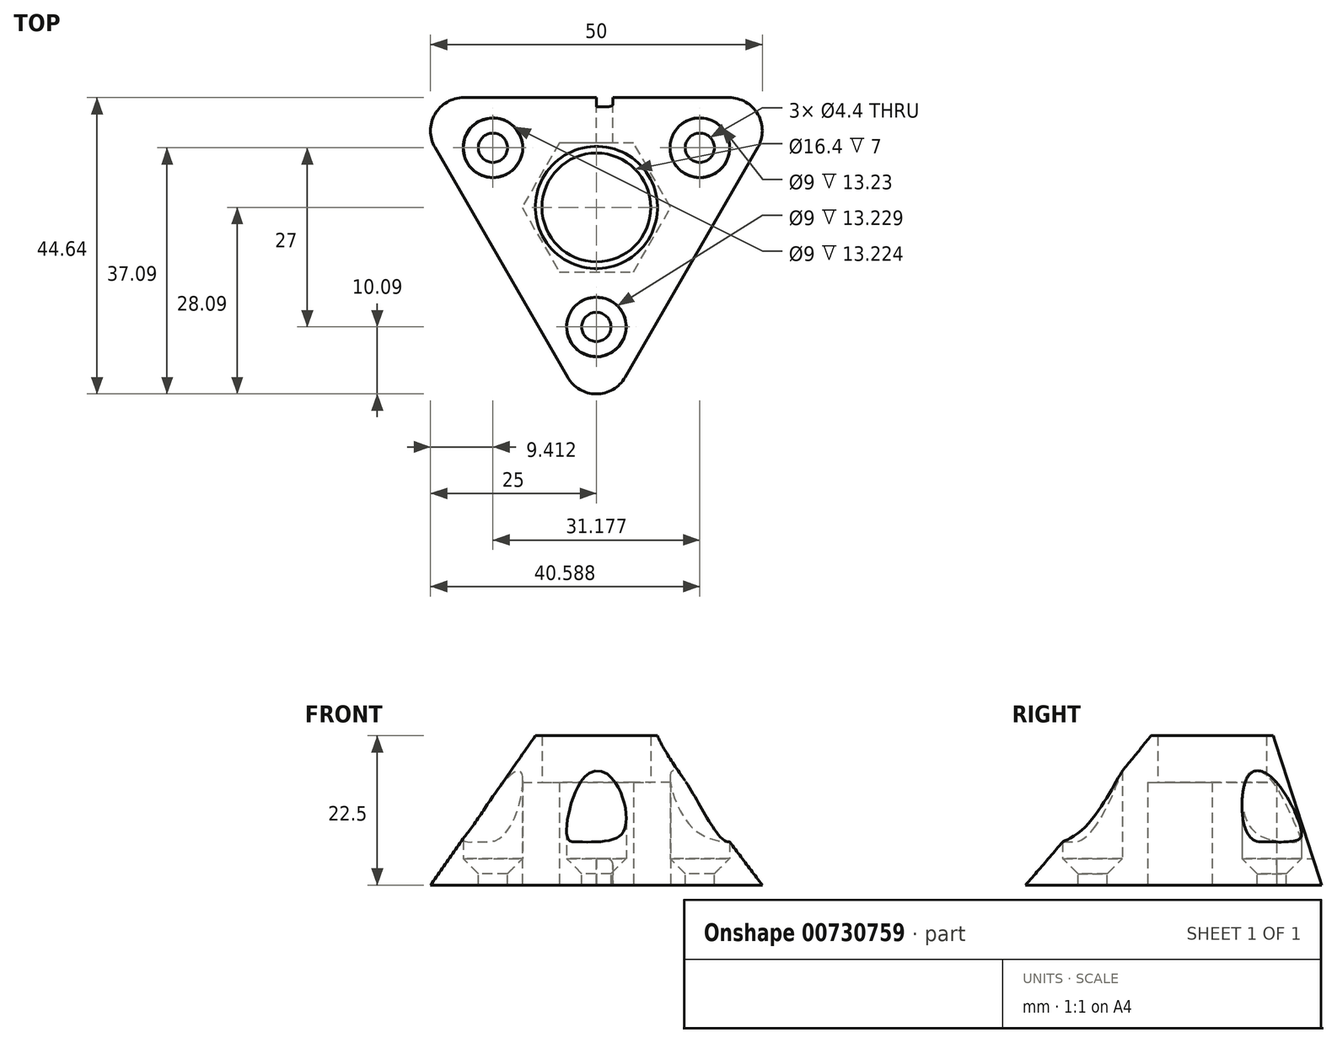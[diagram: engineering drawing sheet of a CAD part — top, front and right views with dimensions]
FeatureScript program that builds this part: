
annotation { "Feature Type Name" : "Feature", "Feature Type Description" : "" }
export const myFeature = defineFeature(function(context is Context, id is Id, definition is map)
    precondition{}
    {
        {
            var Q0;
            Q0=qCreatedBy(makeId("Top.planeOp"),FACE);
            var sketch = newSketch(context, id + "F0", { "sketchPlane" : qUnion([Q0])});
            skCircle(sketch, "E0.cCircle", {"center": v(0, 0) * mm, "radius": 16.55 * mm, "construction": true});
            skLineSegment(sketch, "E0.0", {"start": v(24.33, 9.05) * mm, "end": v(4.33, -25.6) * mm});
            skLineSegment(sketch, "E0.1", {"start": v(-4.33, -25.6) * mm, "end": v(-24.33, 9.05) * mm});
            skLineSegment(sketch, "E0.2", {"start": v(-20, 16.55) * mm, "end": v(20, 16.55) * mm});
            skPoint(sketch, "E0.0.midPoint", {"position": v(14.33, -8.27) * mm});
            skPoint(sketch, "E1.visualSharp", {"position": v(-28.66, 16.55) * mm});
            skArc(sketch, "E1.filletArc", {"start": v(-20, 16.55) * mm, "mid": v(-24.33, 14.05) * mm, "end": v(-24.33, 9.05) * mm});
            skPoint(sketch, "E2.visualSharp", {"position": v(28.66, 16.55) * mm});
            skArc(sketch, "E2.filletArc", {"start": v(24.33, 9.05) * mm, "mid": v(24.33, 14.05) * mm, "end": v(20, 16.55) * mm});
            skPoint(sketch, "E3.visualSharp", {"position": v(0, -33.1) * mm});
            skArc(sketch, "E3.filletArc", {"start": v(-4.33, -25.6) * mm, "mid": v(0, -28.1) * mm, "end": v(4.33, -25.6) * mm});
            skSolve(sketch);
        }
        {
            var Q0;
            Q0=qCreatedBy(makeId("Top.planeOp"),FACE);
            cPlane(context, id + "F1", {"entities" : qUnion([Q0]), "cplaneType" : CPlaneType.OFFSET, "offset" : 22.5 * mm, "width" : 150 * mm, "height" : 150 * mm});
        }
        {
            var Q0;
            Q0=qCreatedBy(id+"F1.planeOp",FACE);
            var sketch = newSketch(context, id + "F2", { "sketchPlane" : qUnion([Q0])});
            skCircle(sketch, "E4", {"center": v(0, 0) * mm, "radius": 9.2 * mm});
            skSolve(sketch);
        }
        {
            var Q0;
            Q0=makeQuery(id+"F0.imprint","IMPRINT",FACE,{"disambiguationData":[TD([[makeQuery(id+"F0.imprint","IMPRINT",EDGE,{"derivedFrom":sQuery(id+"F0.wireOp",EDGE,"E0.0")}),-1.0]])]});
            var Q1;
            Q1=makeQuery(id+"F2.imprint","IMPRINT",FACE,{"disambiguationData":[TD([[makeQuery(id+"F2.imprint","IMPRINT",EDGE,{"derivedFrom":sQuery(id+"F2.wireOp",EDGE,"E4")}),1.0]])]});
            loft(context, id + "F3", {"sheetProfilesArray" : [{ "sheetProfileEntities" : qUnion([Q0]) }, { "sheetProfileEntities" : qUnion([Q1]) }]});
        }
        {
            var Q0;
            Q0=makeQuery(id+"F3.opLoft","CAP_FACE",FACE,{"disambiguationData":[OSD([makeQuery(id+"F0.imprint","IMPRINT",FACE,{"disambiguationData":[TD([[makeQuery(id+"F0.imprint","IMPRINT",EDGE,{"derivedFrom":sQuery(id+"F0.wireOp",EDGE,"E0.0")}),-1.0]])]})])],"isStart":true});
            var sketch = newSketch(context, id + "F4", { "sketchPlane" : qUnion([Q0])});
            skCircle(sketch, "E5", {"center": v(0, 0) * mm, "radius": 8.2 * mm});
            skCircle(sketch, "E6.cCircle", {"center": v(0, 0) * mm, "radius": 9.7 * mm, "construction": true});
            skLineSegment(sketch, "E6.0", {"start": v(-5.6, 9.7) * mm, "end": v(5.6, 9.7) * mm});
            skLineSegment(sketch, "E6.1", {"start": v(5.6, 9.7) * mm, "end": v(11.2, 0) * mm});
            skLineSegment(sketch, "E6.2", {"start": v(11.2, 0) * mm, "end": v(5.6, -9.7) * mm});
            skLineSegment(sketch, "E6.3", {"start": v(5.6, -9.7) * mm, "end": v(-5.6, -9.7) * mm});
            skLineSegment(sketch, "E6.4", {"start": v(-5.6, -9.7) * mm, "end": v(-11.2, 0) * mm});
            skLineSegment(sketch, "E6.5", {"start": v(-11.2, 0) * mm, "end": v(-5.6, 9.7) * mm});
            skPoint(sketch, "E6.0.midPoint", {"position": v(0, 9.7) * mm});
            skLineSegment(sketch, "E7.bottom", {"start": v(0, -9.7) * mm, "end": v(-2.5, -9.7) * mm});
            skLineSegment(sketch, "E7.top", {"start": v(0, -16.55) * mm, "end": v(-2.5, -16.55) * mm});
            skLineSegment(sketch, "E7.left", {"start": v(0, -9.7) * mm, "end": v(0, -16.55) * mm});
            skLineSegment(sketch, "E7.right", {"start": v(-2.5, -9.7) * mm, "end": v(-2.5, -16.55) * mm});
            skLineSegment(sketch, "E8.MirrorCS", {"start": v(2.5, -9.7) * mm, "end": v(2.5, -16.55) * mm});
            skSolve(sketch);
        }
        {
            var Q0;
            Q0=makeQuery(id+"F4.imprint","IMPRINT",FACE,{"disambiguationData":[TD([[makeQuery(id+"F4.imprint","IMPRINT",EDGE,{"derivedFrom":sQuery(id+"F4.wireOp",EDGE,"E5")}),1.0]])]});
            extrude(context, id + "F5", {"entities" : qUnion([Q0]), "operationType" : NewBodyOperationType.REMOVE, "endBound" : BoundingType.UP_TO_NEXT, "oppositeDirection" : true, "depth" : 25 * mm, "offsetDistance" : 25 * mm});
        }
        {
            var Q0;
            Q0=makeQuery(id+"F4.imprint","IMPRINT",FACE,{"disambiguationData":[TD([[makeQuery(id+"F4.imprint","IMPRINT",EDGE,{"derivedFrom":sQuery(id+"F4.wireOp",EDGE,"E5")}),-1.0]])]});
            extrude(context, id + "F6", {"entities" : qUnion([Q0]), "operationType" : NewBodyOperationType.REMOVE, "oppositeDirection" : true, "depth" : 15.5 * mm, "offsetDistance" : 25 * mm});
        }
        {
            var Q0;
            Q0=qCreatedBy(makeId("Top.planeOp"),FACE);
            cPlane(context, id + "F7", {"entities" : qUnion([Q0]), "cplaneType" : CPlaneType.OFFSET, "offset" : 4 * mm, "width" : 150 * mm, "height" : 150 * mm});
        }
        {
            var Q0;
            Q0=qCreatedBy(id+"F7.planeOp",FACE);
            var sketch = newSketch(context, id + "F8", { "sketchPlane" : qUnion([Q0])});
            skPoint(sketch, "E9", {"position": v(0, -18) * mm});
            skPoint(sketch, "E10.1.0", {"position": v(15.59, 9) * mm});
            skPoint(sketch, "E10.2.0", {"position": v(-15.59, 9) * mm});
            skPoint(sketch, "E10.center", {"position": v(0, 0) * mm});
            skSolve(sketch);
        }
        {
            var Q0;
            Q0=sQuery(id+"F8.wireOp",VERTEX,"E10.2.0");
            var Q1;
            Q1=sQuery(id+"F8.wireOp",VERTEX,"E9");
            var Q2;
            Q2=sQuery(id+"F8.wireOp",VERTEX,"E10.1.0");
            var Q3;
            Q3=makeQuery(id+"F3.opLoft","SWEPT_BODY",BODY,{"disambiguationData":[OSD([makeQuery(id+"F0.imprint","IMPRINT",FACE,{"disambiguationData":[TD([[makeQuery(id+"F0.imprint","IMPRINT",EDGE,{"derivedFrom":sQuery(id+"F0.wireOp",EDGE,"E0.0")}),-1.0]])]}),makeQuery(id+"F2.imprint","IMPRINT",FACE,{"disambiguationData":[TD([[makeQuery(id+"F2.imprint","IMPRINT",EDGE,{"derivedFrom":sQuery(id+"F2.wireOp",EDGE,"E4")}),1.0]])]})])]});
            hole(context, id + "F9", {"style" : HoleStyle.C_SINK, "endStyle" : HoleEndStyle.BLIND, "standardTappedOrClearance" : lookupTablePath({ "standard" : "ISO", "fit" : "Normal", "size" : "M4", "type" : "Clearance" }), "standardBlindInLast" : lookupTablePath({ "fit" : "Standard", "standard" : "ISO", "size" : "M4", "type" : "Clearance" }), "holeDiameter" : 4.4 * mm, "cSinkDiameter" : 8.96 * mm, "cSinkAngle" : 90 * degree, "majorDiameter" : 4 * mm, "holeDepth" : 14.1 * mm, "isTappedThrough" : true, "tappedDepth" : 12 * mm, "tapClearance" : 3, "locations" : qUnion([Q0, Q1, Q2]), "scope" : qUnion([Q3])});
        }
        {
            var Q0;
            Q0=sQuery(id+"F8.wireOp",VERTEX,"E10.2.0");
            var Q1;
            Q1=sQuery(id+"F8.wireOp",VERTEX,"E9");
            var Q2;
            Q2=sQuery(id+"F8.wireOp",VERTEX,"E10.1.0");
            var Q3;
            Q3=makeQuery(id+"F3.opLoft","SWEPT_BODY",BODY,{"disambiguationData":[OSD([makeQuery(id+"F0.imprint","IMPRINT",FACE,{"disambiguationData":[TD([[makeQuery(id+"F0.imprint","IMPRINT",EDGE,{"derivedFrom":sQuery(id+"F0.wireOp",EDGE,"E0.0")}),-1.0]])]}),makeQuery(id+"F2.imprint","IMPRINT",FACE,{"disambiguationData":[TD([[makeQuery(id+"F2.imprint","IMPRINT",EDGE,{"derivedFrom":sQuery(id+"F2.wireOp",EDGE,"E4")}),1.0]])]})])]});
            hole(context, id + "F10", {"style" : HoleStyle.SIMPLE, "endStyle" : HoleEndStyle.BLIND, "oppositeDirection" : true, "holeDiameter" : 9 * mm, "majorDiameter" : 5 * mm, "holeDepth" : 14.1 * mm, "isTappedThrough" : true, "tappedDepth" : 12 * mm, "tapClearance" : 3, "locations" : qUnion([Q0, Q1, Q2]), "scope" : qUnion([Q3])});
        }
        {
            var Q0;
            Q0=makeQuery(id+"F4.imprint","IMPRINT",FACE,{"disambiguationData":[TD([[makeQuery(id+"F4.imprint","IMPRINT",EDGE,{"derivedFrom":sQuery(id+"F4.wireOp",EDGE,"E7.bottom")}),1.0]])]});
            var Q1;
            {var subQ0=sQuery(id+"F4.wireOp",EDGE,"E7.left");Q1=makeQuery(id+"F4.imprint","IMPRINT",FACE,{"disambiguationData":[TD([[makeQuery(id+"F4.imprint","IMPRINT",EDGE,{"derivedFrom":subQ0}),1.0]])]});}
            extrude(context, id + "F11", {"entities" : qUnion([Q0, Q1]), "operationType" : NewBodyOperationType.REMOVE, "oppositeDirection" : true, "depth" : 4 * mm, "offsetDistance" : 25 * mm});
        }
        {
            var Q0;
            Q0=makeQuery(id+"F11.boolean.opBoolean","COPY",EDGE,{"derivedFrom":makeQuery(id+"F11.opExtrude","CAP_EDGE",EDGE,{"disambiguationData":[OSD([sQuery(id+"F4.wireOp",EDGE,"E7.right")])],"isStart":false})});
            var Q1;
            Q1=makeQuery(id+"F11.boolean.opBoolean","COPY",EDGE,{"derivedFrom":makeQuery(id+"F11.opExtrude","CAP_EDGE",EDGE,{"disambiguationData":[OSD([sQuery(id+"F4.wireOp",EDGE,"E8.MirrorCS")])],"isStart":false})});
            fillet(context, id + "F12", {"entities" : qUnion([Q0, Q1]), "radius" : 1 * mm, "tangentPropagation" : true, "allowEdgeOverflow" : false});
        }
    });
